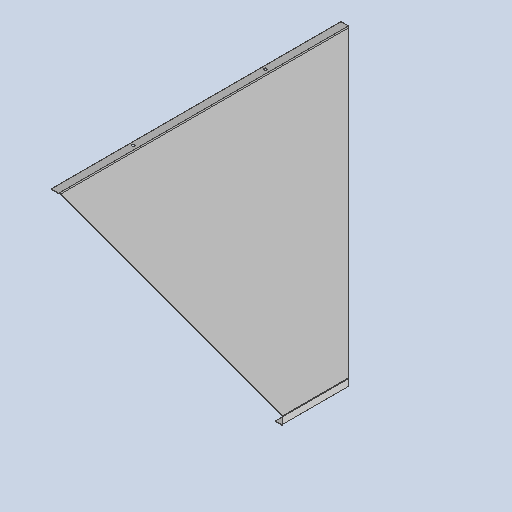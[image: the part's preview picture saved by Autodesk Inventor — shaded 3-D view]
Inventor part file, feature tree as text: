
AUTODESK INVENTOR PART (.ipt)
format: ipt  version: 2025 (Build 290162010, 162A)  size: 336,384 bytes
history: native  units: mm
features: sheet_metal_op x9, sketch x8, other x7, extrude x3, mirror x1, pattern_linear x1, projected_geometry x1
ambient origin geometry x8: Origin, YZ Plane, XZ Plane, XY Plane, X Axis, Y Axis, Z Axis, Center Point
bodies: Body1 (feature_tree)
feature tree (30):
  sheet_metal_op  "Contour Flange2"
  extrude  "Extrusion7"  Depth=8.0mm
  extrude  "Extrusion11"  Depth=3.0mm
  other  "A-Side Definition"
  extrude  "Extrusion15"  Depth=3.0mm
  mirror  "Mirror1"
  sheet_metal_op  "Flange3"
  sheet_metal_op  "Flange4"
  pattern_linear  "Rectangular Pattern1"  Count1=174  [1 undecoded]
  sketch  "Sketch1"  dims[d0=1170.0mm d63=8.0mm]
  other  "Plate4"
  sheet_metal_op  "Bend4"
  sheet_metal_op  "Corner4"
  sketch  "Sketch10"  dims[d64=0.0mm d66=3.0mm]
  sketch  "Sketch14"  dims[d67=3.0mm d68=1.5mm]
  sketch  "Sketch20"  dims[d69=6.0mm]
  projected_geometry  "Projected Loop13"
  sketch  "Sketch21"  dims[d70=5.0mm d71=1740.0mm]
  other  "Plate5"
  sheet_metal_op  "Bend5"
  sheet_metal_op  "Corner5"
  sketch  "Sketch22"  dims[d72=5.0mm]
  other  "Plate6"
  sheet_metal_op  "Bend6"
  sheet_metal_op  "Corner6"
  sketch  "Sketch23"  dims[d73=4.0mm]
  sketch  "Sketch24"  dims[d74=12.0mm d75=3.0mm d76=5.0mm d81=10.0mm d82=0.0mm d99=76.5mm d100=0.0mm d101=0.0mm d102=60.0mm d110=3.0mm d111=400.0mm d120=120.0deg d121=175.0mm d122=8.0mm d123=0.0mm d124=850.499815mm d125=50.0mm d126=3.0mm d127=1.5mm d128=6.0mm d129=5.0mm d130=50.0mm d131=30.0deg d132=5.0mm d133=12.0mm d134=3.0mm d135=5.0mm d136=3.0mm d137=1.5mm d138=6.0mm d139=5.0mm d140=45.0mm d141=90.0deg d142=5.0mm d143=12.0mm d144=3.0mm d145=5.0mm d146=14.0mm d147=20.0mm d148=3.0mm d149=0.0mm d150=30.0mm d152=160.0mm d153=16.0mm d154=800.0mm d155=20.0mm d156=3.0mm d157=0.0mm]
  other  "Cut1"
  other  "Cut2"
  other  "Definition1"
note: 1 required parameter value undecoded (feature->parameter linkage not recoverable at this tier; creation-order binding heuristic only, values carry confidence <= 0.55)
